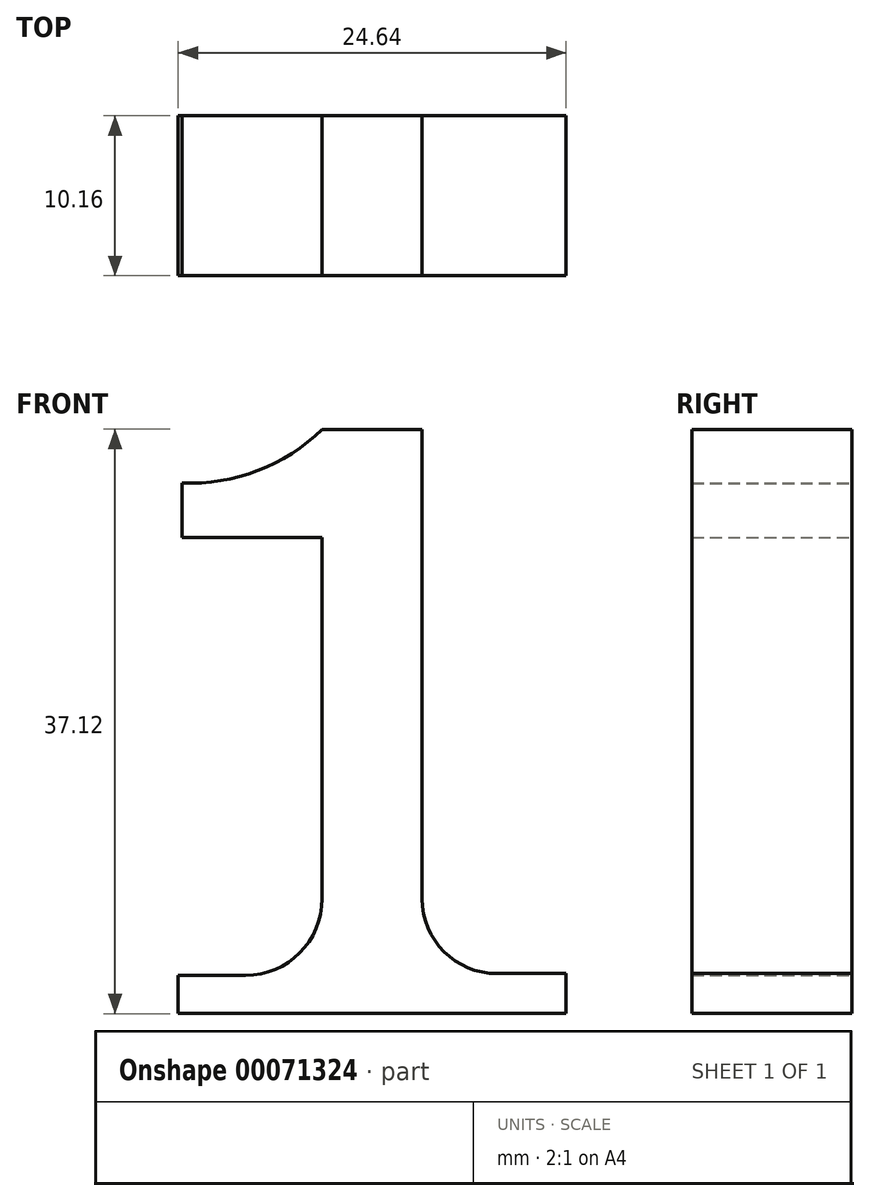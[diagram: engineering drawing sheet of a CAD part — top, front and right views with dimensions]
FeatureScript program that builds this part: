
annotation { "Feature Type Name" : "Feature", "Feature Type Description" : "" }
export const myFeature = defineFeature(function(context is Context, id is Id, definition is map)
    precondition{}
    {
        {
            var Q0;
            Q0=qCreatedBy(makeId("Front.planeOp"),FACE);
            var sketch = newSketch(context, id + "F0", { "sketchPlane" : qUnion([Q0])});
            skLineSegment(sketch, "E0.rect.top", {"start": v(3.18, 17.29) * mm, "end": v(-3.18, 17.29) * mm});
            skLineSegment(sketch, "E0.rect.left", {"start": v(3.18, -12.53) * mm, "end": v(3.18, 17.29) * mm});
            skLineSegment(sketch, "E0.rect.right", {"start": v(-3.18, -12.53) * mm, "end": v(-3.18, 10.43) * mm});
            skPoint(sketch, "E0.rect.middle", {"position": v(0, 0) * mm});
            skLineSegment(sketch, "E1.bottom", {"start": v(7.93, -17.29) * mm, "end": v(12.32, -17.29) * mm});
            skLineSegment(sketch, "E1.top", {"start": v(0, -19.83) * mm, "end": v(12.32, -19.83) * mm});
            skLineSegment(sketch, "E1.right", {"start": v(12.32, -17.29) * mm, "end": v(12.32, -19.83) * mm});
            skLineSegment(sketch, "E2.MirrorCS", {"start": v(-12.32, -17.29) * mm, "end": v(-12.32, -19.83) * mm});
            skLineSegment(sketch, "E3.MirrorCS", {"start": v(0, -19.83) * mm, "end": v(-12.32, -19.83) * mm});
            skLineSegment(sketch, "E4.bottom", {"start": v(-3.17, 10.43) * mm, "end": v(-12.07, 10.43) * mm});
            skLineSegment(sketch, "E4.right", {"start": v(-12.07, 10.43) * mm, "end": v(-12.07, 13.87) * mm});
            skArc(sketch, "E5", {"start": v(-12.07, 13.87) * mm, "mid": v(-7.27, 14.66) * mm, "end": v(-3.18, 17.29) * mm});
            skArc(sketch, "E6", {"start": v(-8.04, -17.4) * mm, "mid": v(-4.6, -15.98) * mm, "end": v(-3.18, -12.53) * mm});
            skArc(sketch, "E7.MirrorCS", {"start": v(7.93, -17.29) * mm, "mid": v(4.5, -15.82) * mm, "end": v(3.18, -12.32) * mm});
            skLineSegment(sketch, "E8.trimOffspring", {"start": v(-8.04, -17.4) * mm, "end": v(-12.35, -17.4) * mm});
            skPoint(sketch, "E9.MirrorCS.start.orphan", {"position": v(0, -17.4) * mm});
            skPoint(sketch, "E10.orphan", {"position": v(0, -17.29) * mm});
            skPoint(sketch, "E0.rect.bottom.end.orphan", {"position": v(-3.18, -17.29) * mm});
            skPoint(sketch, "E11.orphan", {"position": v(3.18, -17.29) * mm});
            skSolve(sketch);
        }
        {
            var Q0;
            Q0 = qSketchRegion(id + "F0", true);
            extrude(context, id + "F1", {"entities" : qUnion([Q0]), "depth" : 10.16 * mm});
        }
    });
